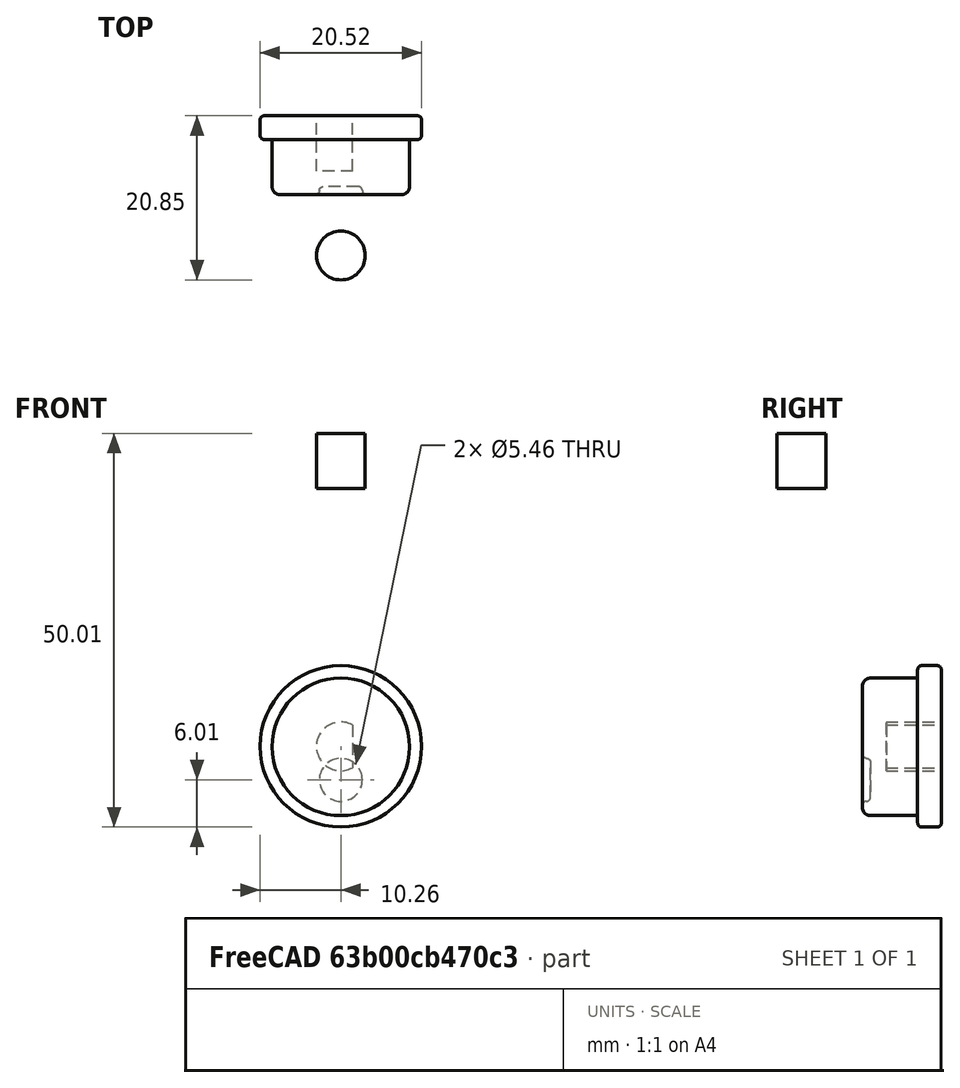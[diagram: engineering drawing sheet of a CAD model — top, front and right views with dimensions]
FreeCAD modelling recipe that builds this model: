
FCSTD DOCUMENT  (FreeCAD 0.15R4671 (Git))
Label: Knob
License: All rights reserved
LicenseURL: http://en.wikipedia.org/wiki/All_rights_reserved
objects: Sketcher::SketchObject×5, PartDesign::Pad×3, PartDesign::Fillet×3, PartDesign::Pocket×2, Mesh::Feature×1
note: 18 computed .brp shape members not serialized (recipe doc carries the construction recipe); baked Part::Feature solids carry a one-line shape summary decoded from their .brp

FEATURE [Mesh::Feature] geetech_graphic_smart_controller
  Placement = pos=(47,0.813467,-43.409) rot=(-0.577349,0.577351,-0.577351;4.18878rad)
FEATURE [Sketcher::SketchObject] Sketch
  Placement = pos=(0,-15,0) rot=(-1,0,0;4.71239rad)
  sketch-geometry (1):
    g0: Circle CenterX=17 CenterY=-32.75 CenterZ=0 NormalX=0 NormalY=0 NormalZ=1 Radius=10.2557
FEATURE [PartDesign::Pad] Pad
  Length = 3
  Length2 = 100
  Placement = pos=(0,-15,0) rot=(-1,0,0;4.71239rad)
  Sketch = -> Sketch
  Type = 0
FEATURE [PartDesign::Fillet] Fillet
  Base = -> Pad [Edge3,Edge2]
  Placement = pos=(0,-15,0) rot=(-1,0,0;4.71239rad)
  Radius = 0.5
FEATURE [Sketcher::SketchObject] Sketch001
  Placement = pos=(0,-18,0) rot=(1,0,0;1.5708rad)
  Support = -> Fillet [Face5]
  sketch-geometry (1):
    g0: Circle CenterX=17 CenterY=-32.8146 CenterZ=0 NormalX=0 NormalY=0 NormalZ=1 Radius=8.73445
FEATURE [PartDesign::Pad] Pad001
  Length = 7
  Length2 = 100
  Placement = pos=(0,-15,0) rot=(-1,0,0;4.71239rad)
  Sketch = -> Sketch001
  Type = 0
FEATURE [PartDesign::Fillet] Fillet001
  Base = -> Pad001 [Edge1]
  Placement = pos=(0,-15,0) rot=(-1,0,0;4.71239rad)
  Radius = 1
FEATURE [Sketcher::SketchObject] Sketch002
  Placement = pos=(0,-25,0) rot=(1,0,0;1.5708rad)
  Support = -> Fillet001 [Face1]
  sketch-geometry (1):
    g0: Circle CenterX=17 CenterY=-37 CenterZ=0 NormalX=0 NormalY=0 NormalZ=1 Radius=2.73023
FEATURE [PartDesign::Pocket] Pocket
  Length = 1
  Placement = pos=(0,-15,0) rot=(-1,0,0;4.71239rad)
  Sketch = -> Sketch002
  Type = 0
FEATURE [PartDesign::Fillet] Fillet002
  Base = -> Pocket [Edge6,Edge2]
  Placement = pos=(0,-15,0) rot=(-1,0,0;4.71239rad)
  Radius = 0.499
FEATURE [Sketcher::SketchObject] Sketch003
  Placement = pos=(0,-15,0) rot=(-1,0,0;1.5708rad)
  Support = -> Fillet002 [Face12]
  sketch-geometry (1):
    g0: Circle CenterX=17 CenterY=32.75 CenterZ=0 NormalX=0 NormalY=0 NormalZ=1 Radius=3.1
  constraints (1):
    c: Radius(g0) = 3.1
FEATURE [PartDesign::Pocket] Pocket001
  Length = 7
  Placement = pos=(0,-15,0) rot=(-1,0,0;4.71239rad)
  Sketch = -> Sketch003
  Type = 0
FEATURE [Sketcher::SketchObject] Sketch004
  Placement = pos=(0,-15,0) rot=(-1,0,0;1.5708rad)
  Support = -> Pocket001 [Face12]
  sketch-geometry (4):
    g0: LineSegment StartX=18.5 StartY=36.0609 StartZ=0 EndX=21.0578 EndY=36.0609 EndZ=0
    g1: LineSegment StartX=21.0578 StartY=36.0609 StartZ=0 EndX=21.0578 EndY=29.5 EndZ=0
    g2: LineSegment StartX=21.0578 StartY=29.5 StartZ=0 EndX=18.5 EndY=29.5 EndZ=0
    g3: LineSegment StartX=18.5 StartY=29.5 StartZ=0 EndX=18.5 EndY=36.0609 EndZ=0
  constraints (8):
    c: Coincident(g0,g1)
    c: Coincident(g1,g2)
    c: Coincident(g2,g3)
    c: Coincident(g3,g0)
    c: Horizontal(g0)
    c: Horizontal(g2)
    c: Vertical(g1)
    c: Vertical(g3)
FEATURE [PartDesign::Pad] Pad002  label="Knob"
  Length = 7
  Length2 = 100
  Placement = pos=(0,-15,0) rot=(-1,0,0;4.71239rad)
  Reversed = true
  Sketch = -> Sketch004
  Type = 0
